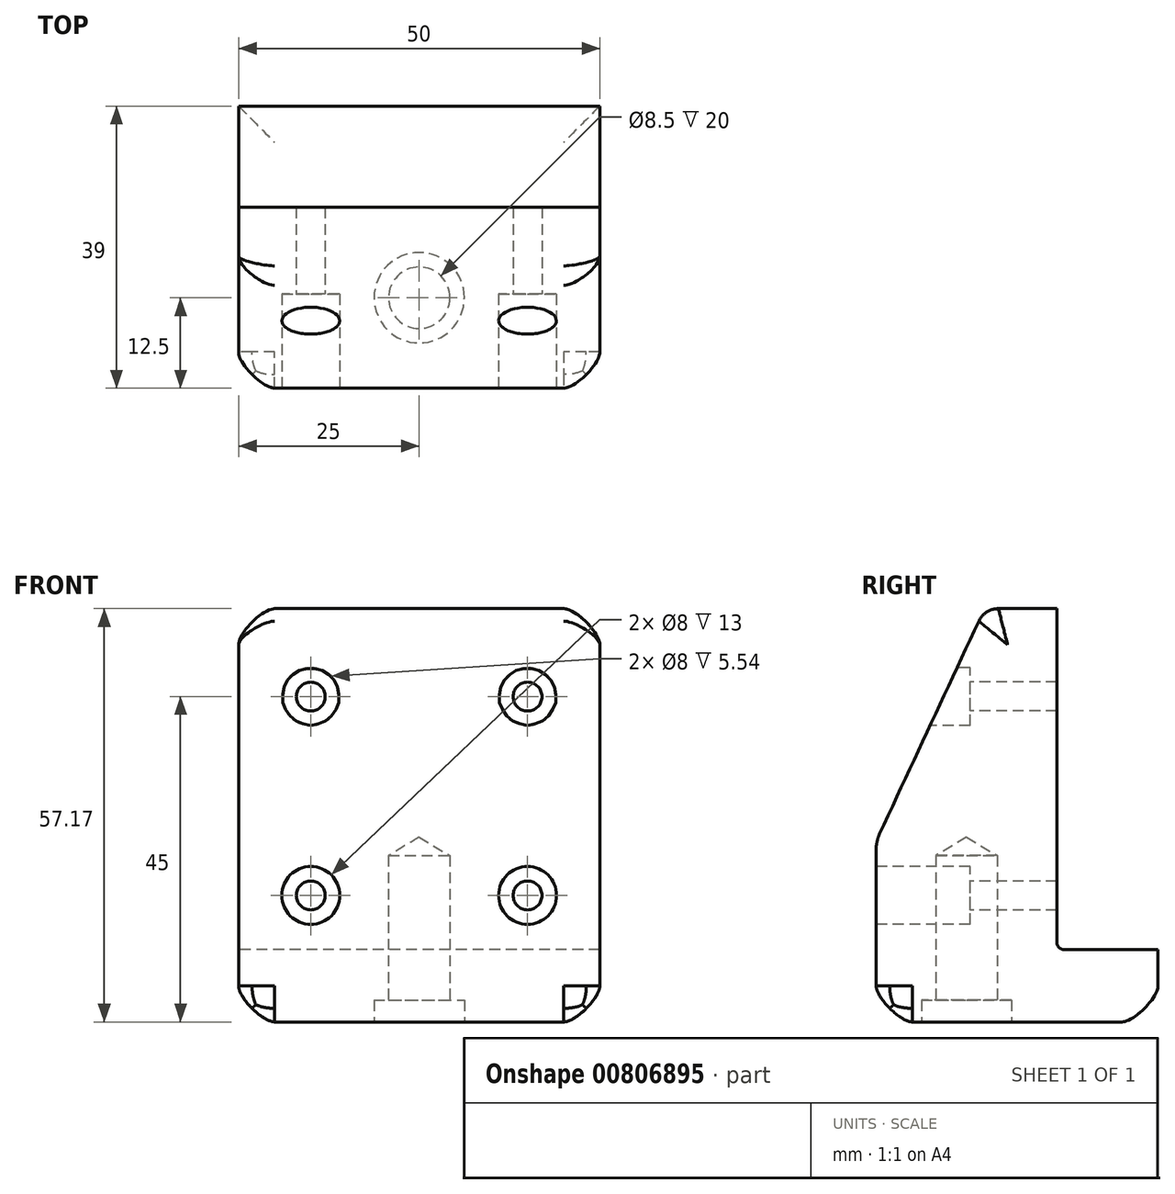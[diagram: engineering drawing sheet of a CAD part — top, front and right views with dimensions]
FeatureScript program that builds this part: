
annotation { "Feature Type Name" : "Feature", "Feature Type Description" : "" }
export const myFeature = defineFeature(function(context is Context, id is Id, definition is map)
    precondition{}
    {
        {
            var Q0;
            Q0=qCreatedBy(makeId("Right.planeOp"),FACE);
            var sketch = newSketch(context, id + "F0", { "sketchPlane" : qUnion([Q0])});
            skLineSegment(sketch, "E0", {"start": v(0, 0) * mm, "end": v(14, 0) * mm});
            skLineSegment(sketch, "E1", {"start": v(14, 0) * mm, "end": v(14, -10) * mm});
            skLineSegment(sketch, "E2", {"start": v(14, -10) * mm, "end": v(-25, -10) * mm});
            skLineSegment(sketch, "E3", {"start": v(-25, -10) * mm, "end": v(-25, 15) * mm});
            skLineSegment(sketch, "E4", {"start": v(-25, 15) * mm, "end": v(-10, 47.17) * mm});
            skLineSegment(sketch, "E5", {"start": v(0, 47.17) * mm, "end": v(0, 0) * mm});
            skLineSegment(sketch, "E6", {"start": v(-10, 47.17) * mm, "end": v(0, 47.17) * mm});
            skPoint(sketch, "E7.orphan", {"position": v(0, 68.61) * mm});
            skSolve(sketch);
        }
        {
            var Q0;
            Q0=makeQuery(id+"F0.imprint","IMPRINT",FACE,{"disambiguationData":[TD([[makeQuery(id+"F0.imprint","IMPRINT",EDGE,{"derivedFrom":sQuery(id+"F0.wireOp",EDGE,"E0")}),-1.0]])]});
            extrude(context, id + "F1", {"entities" : qUnion([Q0]), "endBound" : BoundingType.SYMMETRIC, "depth" : 50 * mm, "offsetDistance" : 25 * mm});
        }
        {
            var Q0;
            Q0=makeQuery(id+"F1.opExtrude","SWEPT_FACE",FACE,{"disambiguationData":[OSD([sQuery(id+"F0.wireOp",EDGE,"E2")])]});
            var sketch = newSketch(context, id + "F2", { "sketchPlane" : qUnion([Q0])});
            skLineSegment(sketch, "E8", {"start": v(0, 0) * mm, "end": v(0, 12.5) * mm, "construction": true});
            skSolve(sketch);
        }
        {
            var Q0;
            Q0=sQuery(id+"F2.wireOp",VERTEX,"E8.end");
            var Q1;
            Q1=makeQuery(id+"F1.opExtrude","SWEPT_BODY",BODY,{"disambiguationData":[OSD([sQuery(id+"F0.wireOp",EDGE,"E0"),sQuery(id+"F0.wireOp",EDGE,"E1"),sQuery(id+"F0.wireOp",EDGE,"E2"),sQuery(id+"F0.wireOp",EDGE,"E3"),sQuery(id+"F0.wireOp",EDGE,"E4"),sQuery(id+"F0.wireOp",EDGE,"E5"),sQuery(id+"F0.wireOp",EDGE,"E6")])]});
            hole(context, id + "F3", {"style" : HoleStyle.C_BORE, "endStyle" : HoleEndStyle.BLIND, "holeDiameter" : 8.5 * mm, "cBoreDiameter" : 12.5 * mm, "cBoreDepth" : 3 * mm, "majorDiameter" : 5 * mm, "holeDepth" : 23 * mm, "isTappedThrough" : true, "tappedDepth" : 12 * mm, "tapClearance" : 3, "startFromSketch" : true, "locations" : qUnion([Q0]), "scope" : qUnion([Q1])});
        }
        {
            var Q0;
            Q0=makeQuery(id+"F1.opExtrude","SWEPT_EDGE",EDGE,{"disambiguationData":[OSD([sQuery(id+"F0.wireOp",EDGE,"E0"),sQuery(id+"F0.wireOp",EDGE,"E5")])]});
            fillet(context, id + "F4", {"entities" : qUnion([Q0]), "radius" : 1 * mm, "tangentPropagation" : true, "allowEdgeOverflow" : false});
        }
        {
            var Q0;
            Q0=makeQuery(id+"F1.opExtrude","SWEPT_EDGE",EDGE,{"disambiguationData":[OSD([sQuery(id+"F0.wireOp",EDGE,"E3"),sQuery(id+"F0.wireOp",EDGE,"E4")])]});
            fillet(context, id + "F5", {"entities" : qUnion([Q0]), "radius" : 5 * mm, "tangentPropagation" : true, "allowEdgeOverflow" : false});
        }
        {
            var Q0;
            Q0=makeQuery(id+"F1.opExtrude","SWEPT_FACE",FACE,{"disambiguationData":[OSD([sQuery(id+"F0.wireOp",EDGE,"E3")])]});
            var sketch = newSketch(context, id + "F6", { "sketchPlane" : qUnion([Q0])});
            skLineSegment(sketch, "E9", {"start": v(0, 0) * mm, "end": v(0, 7.5) * mm, "construction": true});
            skLineSegment(sketch, "E10", {"start": v(0, 7.5) * mm, "end": v(15, 7.5) * mm, "construction": true});
            skLineSegment(sketch, "E11", {"start": v(0, 7.5) * mm, "end": v(-15, 7.5) * mm, "construction": true});
            skSolve(sketch);
        }
        {
            var Q0;
            Q0=sQuery(id+"F6.wireOp",VERTEX,"E11.end");
            var Q1;
            Q1=sQuery(id+"F6.wireOp",VERTEX,"E10.end");
            var Q2;
            Q2=makeQuery(id+"F1.opExtrude","SWEPT_BODY",BODY,{"disambiguationData":[OSD([sQuery(id+"F0.wireOp",EDGE,"E0"),sQuery(id+"F0.wireOp",EDGE,"E1"),sQuery(id+"F0.wireOp",EDGE,"E2"),sQuery(id+"F0.wireOp",EDGE,"E3"),sQuery(id+"F0.wireOp",EDGE,"E4"),sQuery(id+"F0.wireOp",EDGE,"E5"),sQuery(id+"F0.wireOp",EDGE,"E6")])]});
            hole(context, id + "F7", {"style" : HoleStyle.C_BORE, "endStyle" : HoleEndStyle.BLIND, "holeDiameter" : 4 * mm, "cBoreDiameter" : 8 * mm, "cBoreDepth" : 13 * mm, "majorDiameter" : 5 * mm, "holeDepth" : 50 * mm, "isTappedThrough" : true, "tappedDepth" : 12 * mm, "tapClearance" : 3, "startFromSketch" : true, "locations" : qUnion([Q0, Q1]), "scope" : qUnion([Q2])});
        }
        {
            var Q0;
            Q0=qCreatedBy(makeId("Front.planeOp"),FACE);
            cPlane(context, id + "F8", {"entities" : qUnion([Q0]), "cplaneType" : CPlaneType.OFFSET, "offset" : 25 * mm, "width" : 150 * mm, "height" : 150 * mm});
        }
        {
            var Q0;
            Q0=qCreatedBy(id+"F8.planeOp",FACE);
            var sketch = newSketch(context, id + "F9", { "sketchPlane" : qUnion([Q0])});
            skLineSegment(sketch, "E12", {"start": v(0, 0) * mm, "end": v(0, 35) * mm});
            skLineSegment(sketch, "E13", {"start": v(0, 35) * mm, "end": v(15, 35) * mm});
            skLineSegment(sketch, "E14", {"start": v(15, 35) * mm, "end": v(0, 35) * mm});
            skLineSegment(sketch, "E15", {"start": v(-15, 35) * mm, "end": v(0, 35) * mm});
            skCircle(sketch, "E16.0", {"center": v(-15, 7.5) * mm, "radius": 2 * mm});
            skLineSegment(sketch, "E17", {"start": v(-15, 35) * mm, "end": v(-15, 7.5) * mm});
            skSolve(sketch);
        }
        {
            var Q0;
            Q0=sQuery(id+"F9.wireOp",VERTEX,"E13.end");
            var Q1;
            Q1=sQuery(id+"F9.wireOp",VERTEX,"E15.start");
            var Q2;
            Q2=makeQuery(id+"F1.opExtrude","SWEPT_BODY",BODY,{"disambiguationData":[OSD([sQuery(id+"F0.wireOp",EDGE,"E0"),sQuery(id+"F0.wireOp",EDGE,"E1"),sQuery(id+"F0.wireOp",EDGE,"E2"),sQuery(id+"F0.wireOp",EDGE,"E3"),sQuery(id+"F0.wireOp",EDGE,"E4"),sQuery(id+"F0.wireOp",EDGE,"E5"),sQuery(id+"F0.wireOp",EDGE,"E6")])]});
            hole(context, id + "F10", {"style" : HoleStyle.C_BORE, "endStyle" : HoleEndStyle.BLIND, "holeDiameter" : 4 * mm, "cBoreDiameter" : 8 * mm, "cBoreDepth" : 13 * mm, "majorDiameter" : 5 * mm, "holeDepth" : 50 * mm, "isTappedThrough" : true, "tappedDepth" : 12 * mm, "tapClearance" : 3, "startFromSketch" : true, "locations" : qUnion([Q0, Q1]), "scope" : qUnion([Q2])});
        }
        {
            var Q0;
            Q0=makeQuery(id+"F1.opExtrude","SWEPT_EDGE",EDGE,{"disambiguationData":[OSD([sQuery(id+"F0.wireOp",EDGE,"E4"),sQuery(id+"F0.wireOp",EDGE,"E6")])]});
            fillet(context, id + "F11", {"entities" : qUnion([Q0]), "radius" : 3 * mm, "tangentPropagation" : true, "allowEdgeOverflow" : false});
        }
        {
            var Q0;
            Q0=makeQuery(id+"F1.opExtrude","CAP_EDGE",EDGE,{"disambiguationData":[OSD([sQuery(id+"F0.wireOp",EDGE,"E4")])],"isStart":true});
            var Q1;
            Q1=makeQuery(id+"F1.opExtrude","CAP_EDGE",EDGE,{"disambiguationData":[OSD([sQuery(id+"F0.wireOp",EDGE,"E4")])],"isStart":false});
            var Q2;
            Q2=makeQuery(id+"F1.opExtrude","CAP_EDGE",EDGE,{"disambiguationData":[OSD([sQuery(id+"F0.wireOp",EDGE,"E2")])],"isStart":false});
            var Q3;
            Q3=makeQuery(id+"F1.opExtrude","SWEPT_EDGE",EDGE,{"disambiguationData":[OSD([sQuery(id+"F0.wireOp",EDGE,"E2"),sQuery(id+"F0.wireOp",EDGE,"E3")])]});
            var Q4;
            Q4=makeQuery(id+"F1.opExtrude","CAP_EDGE",EDGE,{"disambiguationData":[OSD([sQuery(id+"F0.wireOp",EDGE,"E2")])],"isStart":true});
            var Q5;
            Q5=makeQuery(id+"F1.opExtrude","SWEPT_EDGE",EDGE,{"disambiguationData":[OSD([sQuery(id+"F0.wireOp",EDGE,"E1"),sQuery(id+"F0.wireOp",EDGE,"E2")])]});
            fillet(context, id + "F12", {"entities" : qUnion([Q0, Q1, Q2, Q3, Q4, Q5]), "radius" : 5 * mm, "tangentPropagation" : true, "rho" : 0.25, "crossSection" : FilletCrossSection.CONIC, "allowEdgeOverflow" : false});
        }
    });
